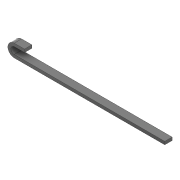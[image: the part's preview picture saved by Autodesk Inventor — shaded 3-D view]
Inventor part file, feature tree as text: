
AUTODESK INVENTOR PART (.ipt)
format: ipt  version: 2020 (Build 240168000, 168)  size: 93,696 bytes
history: native  units: mm
features: extrude x1, sketch x1
ambient origin geometry x8: Origin, YZ Plane, XZ Plane, XY Plane, X Axis, Y Axis, Z Axis, Center Point
bodies: Solid1 (feature_tree)
feature tree (2):
  extrude  "Extrusion1"  Depth=20.0mm
  sketch  "Sketch1"  dims[d0=85.0mm d1=20.0mm d2=20.0mm d4=1000.0mm d5=49.0mm d6=0.0mm d7=68.0mm]
